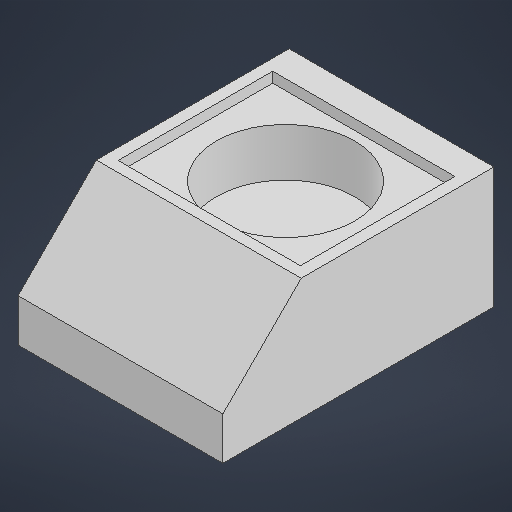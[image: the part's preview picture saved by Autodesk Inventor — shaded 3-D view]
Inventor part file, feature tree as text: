
AUTODESK INVENTOR PART (.ipt)
format: ipt  version: 2025.1 (Build 291241000, 241)  size: 187,392 bytes
history: native  units: mm
features: extrude x4, sketch x2, chamfer x1, projected_geometry x1
ambient origin geometry x8: Origin, YZ Plane, XZ Plane, XY Plane, X Axis, Y Axis, Z Axis, Center Point
bodies: Solid1 (feature_tree)
feature tree (8):
  sketch  "Sketch1"  dims[d2=170.0mm d3=225.0mm]
  extrude  "Extrusion1"  Depth=225.0mm
  extrude  "Extrusion2"  Depth=40.0mm
  chamfer  "Chamfer1"  Distance=5.0mm
  sketch  "Sketch2"  dims[d4=100.5mm d5=0.0mm d9=163.6mm d10=5.0mm d11=138.6mm d12=10.0mm d13=0.0mm d14=65.0mm d15=2.0mm d16=45.0deg d18=151.3mm d19=128.3mm d20=23.0mm d21=115.0mm d22=7.5mm d23=8.6mm d24=0.0mm d25=40.0mm d26=0.0mm]
  extrude  "Extrusion3"  Depth=40.0mm
  extrude  "Extrusion4"  Depth=10.0mm TaperAngle=0.0deg
  projected_geometry  "Projected Loop1"
